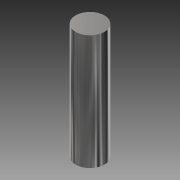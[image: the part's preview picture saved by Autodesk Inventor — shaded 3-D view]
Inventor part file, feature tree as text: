
AUTODESK INVENTOR PART (.ipt)
format: ipt  version: 2013 (Build 170138000, 138)  size: 83,456 bytes
history: native  units: mm
features: extrude x1, sketch x1
ambient origin geometry x8: Origin, YZ Plane, XZ Plane, XY Plane, X Axis, Y Axis, Z Axis, Center Point
bodies: Solid1 (feature_tree)
feature tree (2):
  extrude  "Extrusion1"  Depth=20.0mm TaperAngle=0.0deg
  sketch  "Sketch1"  dims[d0=5.0mm d2=20.0mm d3=0.0mm]
